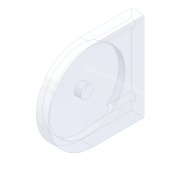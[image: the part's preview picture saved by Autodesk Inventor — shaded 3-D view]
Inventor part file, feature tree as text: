
AUTODESK INVENTOR PART (.ipt)
format: ipt  version: unknown  size: 192,512 bytes
history: native  units: mm
features: sketch x3, extrude x2, revolve x1
ambient origin geometry x8: Origin, YZ Plane, XZ Plane, XY Plane, X Axis, Y Axis, Z Axis, Center Point
feature tree (6):
  revolve  "Revolution1"  [1 undecoded]
  extrude  "Extrusion1"  Depth=12.0mm
  extrude  "Extrusion2"  TaperAngle=90.0deg  [1 undecoded]
  sketch  "Sketch1"  dims[d0=2.0mm d1=2.0mm]
  sketch  "Sketch2"  dims[d2=2.0mm d3=12.0mm]
  sketch  "Sketch3"  dims[d4=2.0mm d5=90.0deg d6=2.5mm d7=10.0mm d8=16.0mm d9=10.0mm d10=0.0mm d11=10.0mm d12=0.0mm]
note: 2 required parameter values undecoded (feature->parameter linkage not recoverable at this tier; creation-order binding heuristic only, values carry confidence <= 0.55)